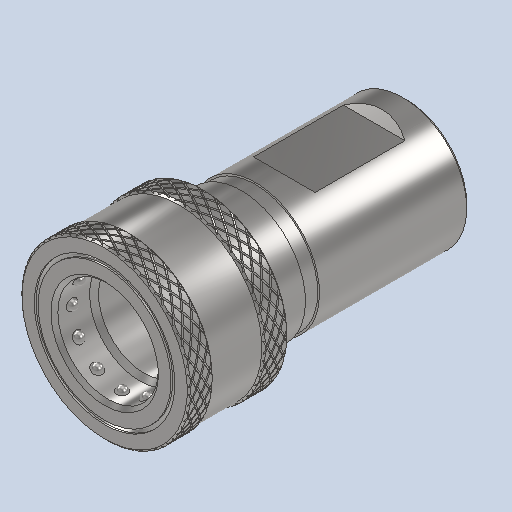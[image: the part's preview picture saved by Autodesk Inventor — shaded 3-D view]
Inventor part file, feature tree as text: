
AUTODESK INVENTOR PART (.ipt)
format: ipt  version: 2022 (Build 260153000, 153)  size: 6,807,040 bytes
history: native  units: in
note: dims shown in document units (in); Inventor stores cm internally (conversion verified against a paired STEP export)
features: other x11, revolve x2, pattern_circular x1
ambient origin geometry x8: Origin, YZ Plane, XZ Plane, XY Plane, X Axis, Y Axis, Z Axis, Center Point
bodies: Solid1 (feature_tree), Solid2 (feature_tree), Solid3 (feature_tree), Solid4 (feature_tree), Solid5 (feature_tree), Solid6 (feature_tree), Solid7 (feature_tree), Solid8 (feature_tree), Solid9 (feature_tree), Solid10 (feature_tree), Solid11 (feature_tree), Solid12 (feature_tree), Solid13 (feature_tree), Solid14 (feature_tree)
feature tree (14):
  revolve  "Revolve1[2]"  [1 undecoded]
  revolve  "Revolve2"  [1 undecoded]
  other  "CirPattern4[1]"
  other  "CirPattern4[2]"
  other  "CirPattern4[3]"
  other  "CirPattern4[4]"
  other  "CirPattern4[5]"
  other  "CirPattern4[6]"
  other  "CirPattern4[7]"
  other  "CirPattern4[8]"
  other  "CirPattern4[9]"
  pattern_circular  "CirPattern5"
  other  "CirPattern4[10]"
  other  "CirPattern4[11]"
note: 2 required parameter values undecoded (feature->parameter linkage not recoverable at this tier; creation-order binding heuristic only, values carry confidence <= 0.55)
